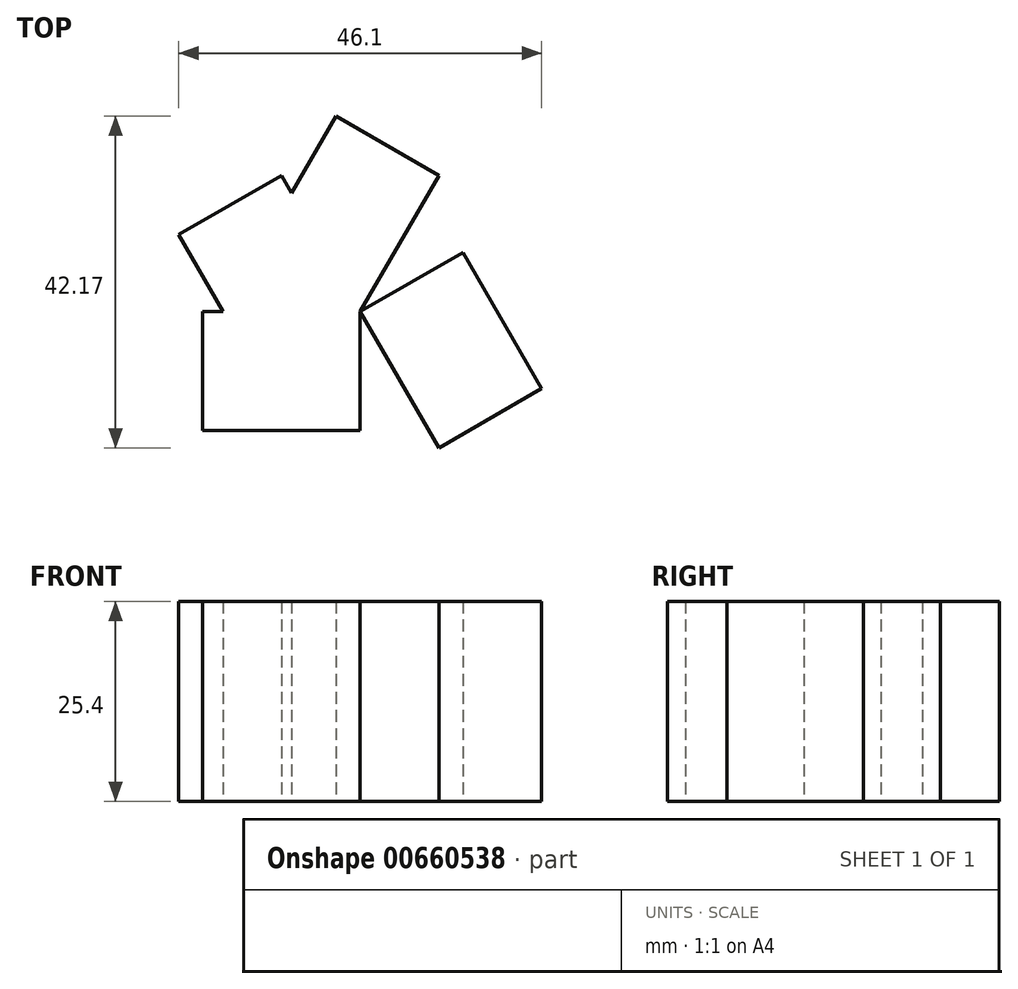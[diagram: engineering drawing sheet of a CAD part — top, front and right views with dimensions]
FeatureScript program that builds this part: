
annotation { "Feature Type Name" : "Feature", "Feature Type Description" : "" }
export const myFeature = defineFeature(function(context is Context, id is Id, definition is map)
    precondition{}
    {
        {
            var Q0;
            Q0=qCreatedBy(makeId("Top.planeOp"),FACE);
            var sketch = newSketch(context, id + "F0", { "sketchPlane" : qUnion([Q0])});
            skLineSegment(sketch, "E0.bottom", {"start": v(0, 0) * mm, "end": v(20, 0) * mm, "construction": true});
            skLineSegment(sketch, "E0.top", {"start": v(0, 15.07) * mm, "end": v(20, 15.07) * mm});
            skLineSegment(sketch, "E0.left", {"start": v(0, 0) * mm, "end": v(0, 15.07) * mm});
            skLineSegment(sketch, "E0.right", {"start": v(20, 0) * mm, "end": v(20, 15.07) * mm});
            skLineSegment(sketch, "E1.1.0", {"start": v(-13.05, 7.53) * mm, "end": v(-3.05, 24.85) * mm});
            skLineSegment(sketch, "E1.1.1", {"start": v(10, 17.32) * mm, "end": v(-3.05, 24.85) * mm});
            skLineSegment(sketch, "E1.1.2", {"start": v(0, 0) * mm, "end": v(-13.05, 7.53) * mm});
            skLineSegment(sketch, "E1.1.3", {"start": v(0, 0) * mm, "end": v(10, 17.32) * mm});
            skLineSegment(sketch, "E1.2.0", {"start": v(-13.05, -7.53) * mm, "end": v(-23.05, 9.79) * mm});
            skLineSegment(sketch, "E1.2.1", {"start": v(-10, 17.32) * mm, "end": v(-23.05, 9.79) * mm});
            skLineSegment(sketch, "E1.2.2", {"start": v(0, 0) * mm, "end": v(-13.05, -7.53) * mm});
            skLineSegment(sketch, "E1.2.3", {"start": v(0, 0) * mm, "end": v(-10, 17.32) * mm});
            skLineSegment(sketch, "E1.3.0", {"start": v(0, -15.07) * mm, "end": v(-20, -15.07) * mm});
            skLineSegment(sketch, "E1.3.1", {"start": v(-20, 0) * mm, "end": v(-20, -15.07) * mm});
            skLineSegment(sketch, "E1.3.2", {"start": v(0, 0) * mm, "end": v(0, -15.07) * mm});
            skLineSegment(sketch, "E1.3.3", {"start": v(0, 0) * mm, "end": v(-20, 0) * mm});
            skLineSegment(sketch, "E1.4.0", {"start": v(13.05, -7.53) * mm, "end": v(3.05, -24.85) * mm, "construction": true});
            skLineSegment(sketch, "E1.4.1", {"start": v(-10, -17.32) * mm, "end": v(3.05, -24.85) * mm});
            skLineSegment(sketch, "E1.4.2", {"start": v(0, 0) * mm, "end": v(13.05, -7.53) * mm});
            skLineSegment(sketch, "E1.4.3", {"start": v(0, 0) * mm, "end": v(-10, -17.32) * mm});
            skLineSegment(sketch, "E1.5.0", {"start": v(13.05, 7.53) * mm, "end": v(23.05, -9.79) * mm});
            skLineSegment(sketch, "E1.5.1", {"start": v(10, -17.32) * mm, "end": v(23.05, -9.79) * mm});
            skLineSegment(sketch, "E1.5.2", {"start": v(0, 0) * mm, "end": v(13.05, 7.53) * mm});
            skLineSegment(sketch, "E1.5.3", {"start": v(0, 0) * mm, "end": v(10, -17.32) * mm});
            skPoint(sketch, "E1.center", {"position": v(0, 0) * mm});
            skSolve(sketch);
        }
        {
            var Q0;
            Q0 = qSketchRegion(id + "F0", true);
            extrude(context, id + "F1", {"entities" : qUnion([Q0]), "depth" : 25.4 * mm, "offsetDistance" : 25.4 * mm});
        }
    });
